# Revit family: QF_Southern Pride_SRG-400
name_source: partatom
category: Specialty Equipment
units: mm (PartAtom-declared; Revit-internal decimal feet)

## family parameters
Always vertical = Yes
Cut with Voids When Loaded = No
OmniClass Number = 23.40.40.00
OmniClass Title = Food Service Equipment and Furnishings
Part Type = Normal
Room Calculation Point = No
Round Connector Dimension = Use Diameter
Shared = No
Work Plane-Based = No

## types (1)
- QF_Southern Pride_SRG-400
    Apparent Power = 1800 VA
    Assembly Code = E1090320
    Box Height = 67.875 "
    CSI MasterFormat = 11 44 00
    Caster Height = 7.5 "
    Conn Plug = NEMA 5-15P
    Cycle = 60 Hz
    Depth = 32.125 "
    Description = Stationary Rack Smoker, Gas-Fired Wood Burning
    Door Height = 51 "
    Door Width = 20 "
    Elec Conn Connection Height = 30.125 "
    FL Amps = 15 A
    Foodservice Equipment Identifier = Yes
    Gas Connection Height = 21 "
    Gas Input = 65000.0 Btu/h
    Gas KW = 19
    Gas Size = 1"
    Manufacturer = Southern Pride
    Model = SRG-400
    Phase = 1
    URL = www.southernpride.com
    URL Cutsheet = https://www.southernpride.com
    Volts = 120 V
    Weight in Pounds = 780
    Width = 40.75 "

## geometry (parser evidence)
native form markers: Sweep x12
no freeform markers — native parametric forms only
